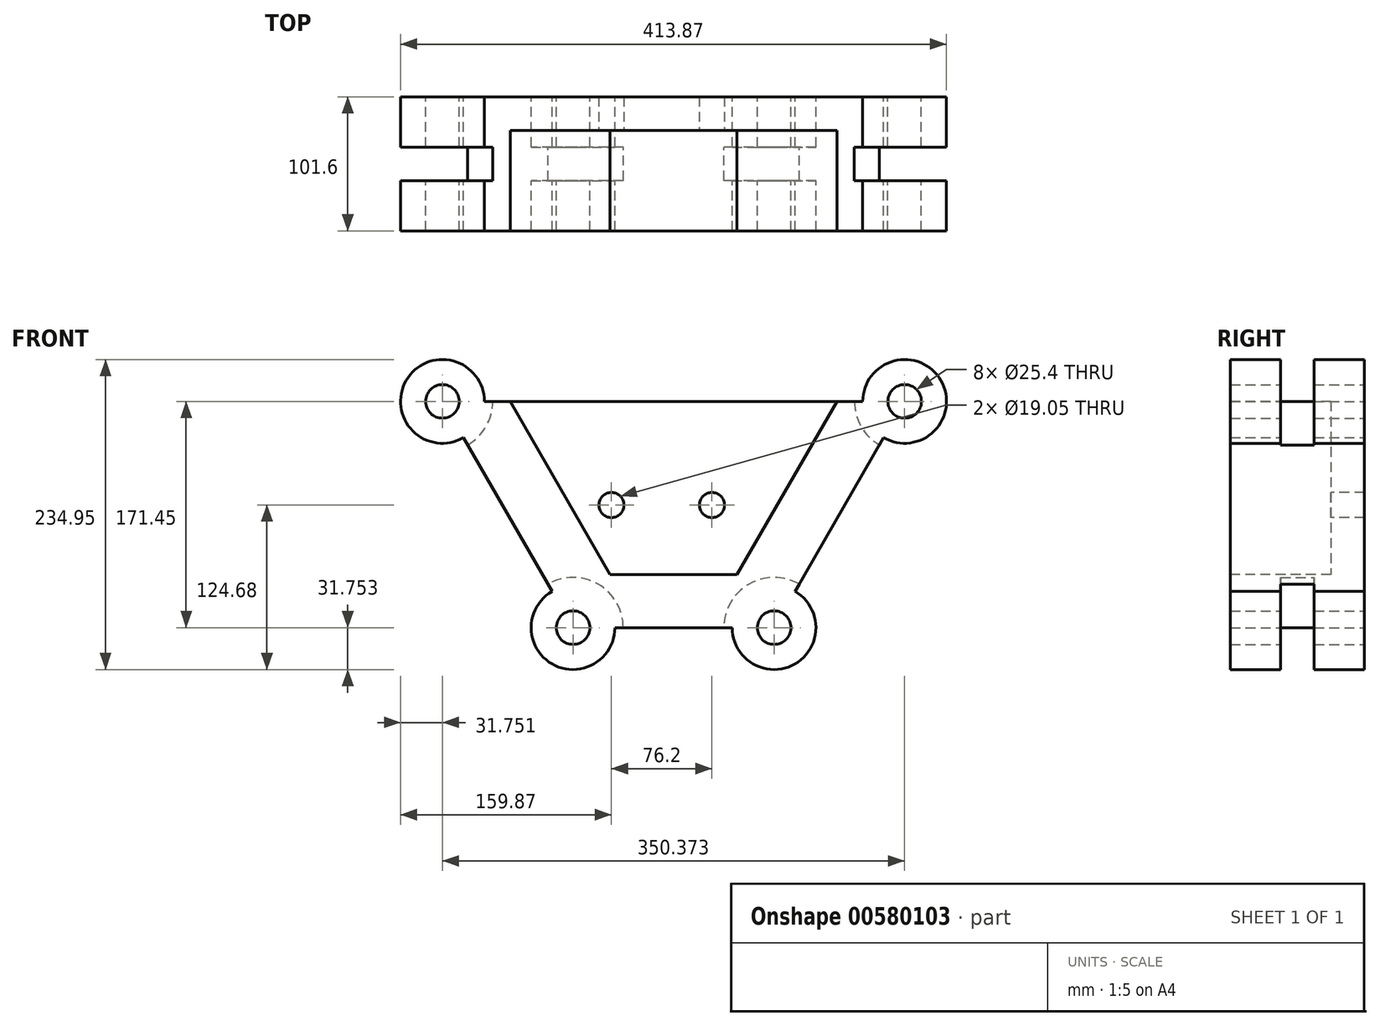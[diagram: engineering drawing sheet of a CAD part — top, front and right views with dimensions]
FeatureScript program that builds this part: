
annotation { "Feature Type Name" : "Feature", "Feature Type Description" : "" }
export const myFeature = defineFeature(function(context is Context, id is Id, definition is map)
    precondition{}
    {
        {
            var Q0;
            Q0=qCreatedBy(makeId("Front.planeOp"),FACE);
            var sketch = newSketch(context, id + "F0", { "sketchPlane" : qUnion([Q0])});
            skLineSegment(sketch, "E0", {"start": v(85.17, -92.93) * mm, "end": v(-67.23, -92.93) * mm});
            skLineSegment(sketch, "E1", {"start": v(-67.23, -92.93) * mm, "end": v(-166.22, 78.52) * mm});
            skLineSegment(sketch, "E2", {"start": v(-166.22, 78.52) * mm, "end": v(184.15, 78.52) * mm});
            skLineSegment(sketch, "E3", {"start": v(184.15, 78.52) * mm, "end": v(85.17, -92.93) * mm});
            skCircle(sketch, "E4", {"center": v(-166.22, 78.52) * mm, "radius": 31.75 * mm});
            skCircle(sketch, "E5", {"center": v(184.15, 78.52) * mm, "radius": 31.75 * mm});
            skCircle(sketch, "E6", {"center": v(-67.23, -92.93) * mm, "radius": 31.75 * mm});
            skCircle(sketch, "E7", {"center": v(85.17, -92.93) * mm, "radius": 31.75 * mm});
            skCircle(sketch, "E8", {"center": v(-67.23, -92.93) * mm, "radius": 12.7 * mm});
            skCircle(sketch, "E9", {"center": v(85.17, -92.93) * mm, "radius": 12.7 * mm});
            skCircle(sketch, "E10", {"center": v(-166.22, 78.52) * mm, "radius": 12.7 * mm});
            skCircle(sketch, "E11", {"center": v(184.15, 78.52) * mm, "radius": 12.7 * mm});
            skSolve(sketch);
        }
        {
            var Q0;
            Q0 = qSketchRegion(id + "F0", true);
            extrude(context, id + "F1", {"entities" : qUnion([Q0]), "endBound" : BoundingType.SYMMETRIC, "depth" : 101.6 * mm, "offsetDistance" : 25.4 * mm});
        }
        {
            var Q0;
            Q0=makeQuery(id+"F1.opExtrude","CAP_FACE",FACE,{"disambiguationData":[OSD([sQuery(id+"F0.wireOp",EDGE,"E0"),sQuery(id+"F0.wireOp",EDGE,"E1"),sQuery(id+"F0.wireOp",EDGE,"E2"),sQuery(id+"F0.wireOp",EDGE,"E3"),sQuery(id+"F0.wireOp",EDGE,"E4"),sQuery(id+"F0.wireOp",EDGE,"E5"),sQuery(id+"F0.wireOp",EDGE,"E6"),sQuery(id+"F0.wireOp",EDGE,"E7"),sQuery(id+"F0.wireOp",EDGE,"E8"),sQuery(id+"F0.wireOp",EDGE,"E9"),sQuery(id+"F0.wireOp",EDGE,"E10"),sQuery(id+"F0.wireOp",EDGE,"E11")])],"isStart":false});
            var sketch = newSketch(context, id + "F2", { "sketchPlane" : qUnion([Q0])});
            skLineSegment(sketch, "E12", {"start": v(-114.9, 78.52) * mm, "end": v(-39.08, -52.78) * mm});
            skLineSegment(sketch, "E13", {"start": v(-39.08, -52.78) * mm, "end": v(57.02, -52.78) * mm});
            skLineSegment(sketch, "E14", {"start": v(57.02, -52.78) * mm, "end": v(132.83, 78.52) * mm});
            skLineSegment(sketch, "E15", {"start": v(132.83, 78.52) * mm, "end": v(-114.9, 78.52) * mm});
            skSolve(sketch);
        }
        {
            var Q0;
            Q0=makeQuery(id+"F2.imprint","IMPRINT",FACE,{"disambiguationData":[TD([[makeQuery(id+"F2.imprint","IMPRINT",EDGE,{"derivedFrom":sQuery(id+"F2.wireOp",EDGE,"E12")}),1.0]])]});
            extrude(context, id + "F3", {"entities" : qUnion([Q0]), "operationType" : NewBodyOperationType.REMOVE, "oppositeDirection" : true, "depth" : 76.2 * mm, "offsetDistance" : 25.4 * mm});
        }
        {
            var Q0;
            Q0=qCreatedBy(makeId("Front.planeOp"),FACE);
            var sketch = newSketch(context, id + "F4", { "sketchPlane" : qUnion([Q0])});
            skCircle(sketch, "E16", {"center": v(-166.22, 78.52) * mm, "radius": 38.1 * mm});
            skCircle(sketch, "E17", {"center": v(-67.23, -92.93) * mm, "radius": 38.1 * mm});
            skCircle(sketch, "E18", {"center": v(85.17, -92.93) * mm, "radius": 38.1 * mm});
            skCircle(sketch, "E19", {"center": v(184.15, 78.52) * mm, "radius": 38.1 * mm});
            skSolve(sketch);
        }
        {
            var Q0;
            Q0 = qSketchRegion(id + "F4", true);
            extrude(context, id + "F5", {"entities" : qUnion([Q0]), "operationType" : NewBodyOperationType.REMOVE, "endBound" : BoundingType.SYMMETRIC, "depth" : 25.4 * mm, "offsetDistance" : 25.4 * mm});
        }
        {
            var Q0;
            Q0=makeQuery(id+"F3.boolean.opBoolean","COPY",FACE,{"derivedFrom":makeQuery(id+"F3.opExtrude","CAP_FACE",FACE,{"disambiguationData":[OSD([sQuery(id+"F2.wireOp",EDGE,"E12"),sQuery(id+"F2.wireOp",EDGE,"E13"),sQuery(id+"F2.wireOp",EDGE,"E14"),sQuery(id+"F2.wireOp",EDGE,"E15")])],"isStart":false})});
            var sketch = newSketch(context, id + "F6", { "sketchPlane" : qUnion([Q0])});
            skCircle(sketch, "E20", {"center": v(-38.1, 0) * mm, "radius": 9.53 * mm});
            skCircle(sketch, "E21", {"center": v(38.1, 0) * mm, "radius": 9.53 * mm});
            skSolve(sketch);
        }
        {
            var Q0;
            Q0 = qSketchRegion(id + "F6", true);
            extrude(context, id + "F7", {"entities" : qUnion([Q0]), "operationType" : NewBodyOperationType.REMOVE, "endBound" : BoundingType.THROUGH_ALL, "oppositeDirection" : true, "depth" : 25.4 * mm, "offsetDistance" : 25.4 * mm});
        }
    });
